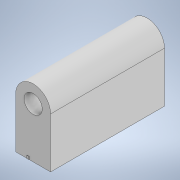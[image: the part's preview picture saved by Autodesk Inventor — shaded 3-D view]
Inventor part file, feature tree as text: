
AUTODESK INVENTOR PART (.ipt)
format: ipt  version: 2021 (Build 250183000, 183)  size: 104,448 bytes
history: native  units: in
note: dims shown in document units (in); Inventor stores cm internally (conversion verified against a paired STEP export)
features: extrude x2, sketch x2
ambient origin geometry x8: Origin, YZ Plane, XZ Plane, XY Plane, X Axis, Y Axis, Z Axis, Center Point
bodies: Solid1 (feature_tree)
feature tree (4):
  extrude  "Extrusion1"  Depth=225.0in
  extrude  "Extrusion2"  Depth=10.0in
  sketch  "Sketch1"  dims[d0=156.0in d1=225.0in]
  sketch  "Sketch2"  dims[d2=510.0in d3=0.0in d4=10.0in d5=1.0in d6=0.0in]
